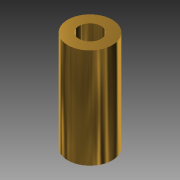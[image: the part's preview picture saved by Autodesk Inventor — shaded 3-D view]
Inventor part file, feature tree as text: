
AUTODESK INVENTOR PART (.ipt)
format: ipt  version: 2015 (Build 190159000, 159)  size: 103,936 bytes
history: native  units: mm
features: extrude x2, sketch x2, other x1
ambient origin geometry x8: Origin, YZ Plane, XZ Plane, XY Plane, X Axis, Y Axis, Z Axis, Center Point
bodies: Body1 (feature_tree)
feature tree (5):
  other  "ソリッド1"
  extrude  "押し出し1"  Depth=8.0mm
  extrude  "押し出し2"  Depth=18.0mm TaperAngle=0.0deg
  sketch  "スケッチ1"
  sketch  "スケッチ2"
